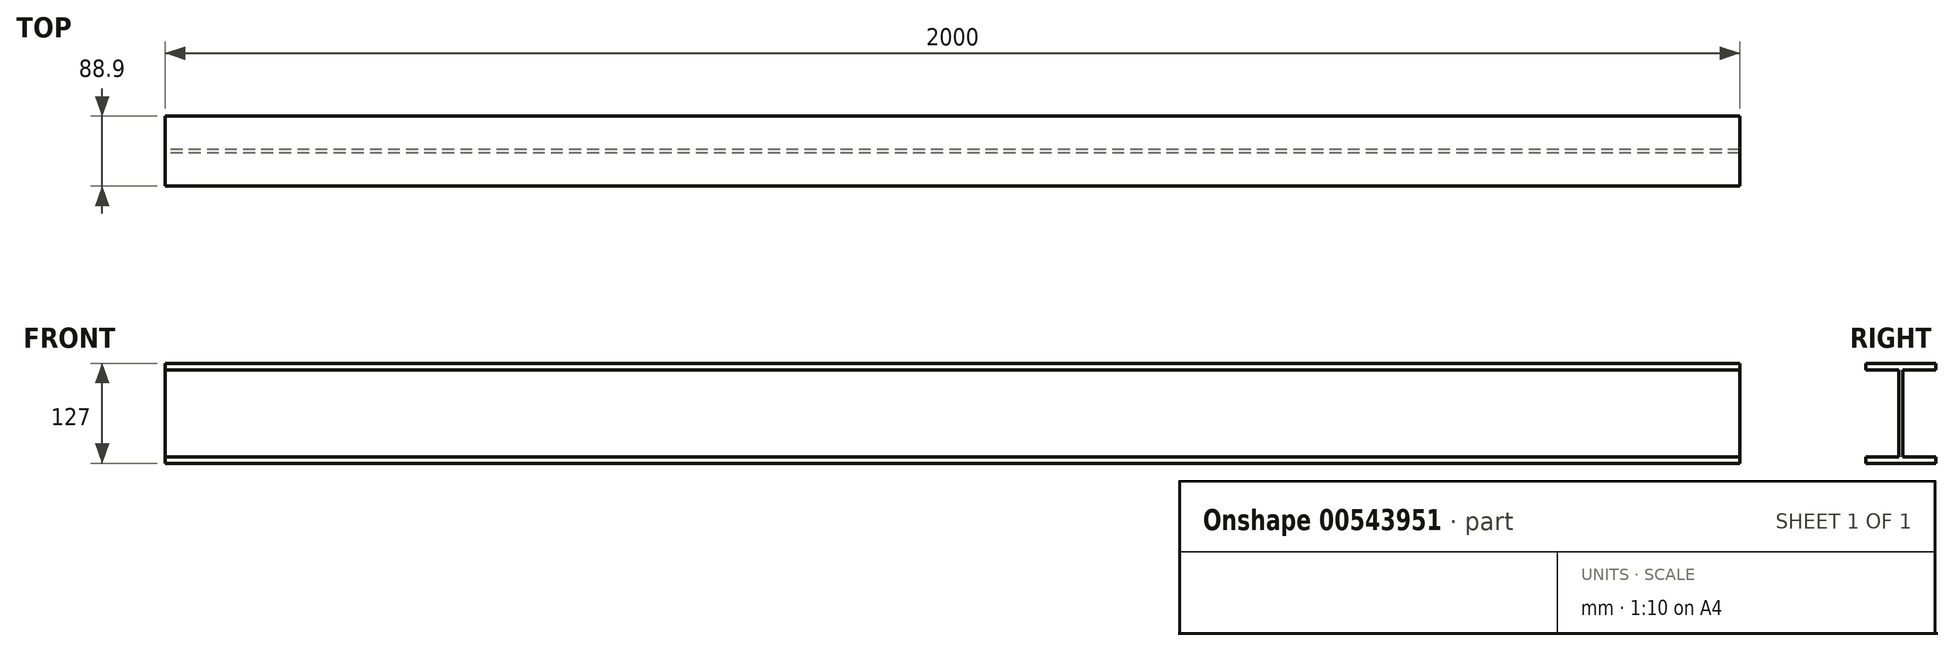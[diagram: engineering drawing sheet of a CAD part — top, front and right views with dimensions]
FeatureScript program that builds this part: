
annotation { "Feature Type Name" : "Feature", "Feature Type Description" : "" }
export const myFeature = defineFeature(function(context is Context, id is Id, definition is map)
    precondition{}
    {
        {
            var Q0;
            Q0=qCreatedBy(makeId("Right.planeOp"),FACE);
            var sketch = newSketch(context, id + "F0", { "sketchPlane" : qUnion([Q0])});
            skLineSegment(sketch, "E0", {"start": v(-44.45, 63.5) * mm, "end": v(44.45, 63.5) * mm});
            skLineSegment(sketch, "E1", {"start": v(44.45, 63.5) * mm, "end": v(44.45, 55.37) * mm});
            skLineSegment(sketch, "E2", {"start": v(44.45, 55.37) * mm, "end": v(2.41, 55.37) * mm});
            skLineSegment(sketch, "E3", {"start": v(2.41, 55.37) * mm, "end": v(2.42, -55.37) * mm});
            skLineSegment(sketch, "E4", {"start": v(2.41, -55.37) * mm, "end": v(44.45, -55.37) * mm});
            skLineSegment(sketch, "E5", {"start": v(44.45, -55.37) * mm, "end": v(44.45, -63.5) * mm});
            skLineSegment(sketch, "E6", {"start": v(44.45, -63.5) * mm, "end": v(-44.45, -63.5) * mm});
            skLineSegment(sketch, "E7", {"start": v(-44.45, -63.5) * mm, "end": v(-44.45, -55.37) * mm});
            skLineSegment(sketch, "E8", {"start": v(-44.45, -55.37) * mm, "end": v(-2.41, -55.37) * mm});
            skLineSegment(sketch, "E9", {"start": v(-2.42, -55.37) * mm, "end": v(-2.42, 55.37) * mm});
            skLineSegment(sketch, "E10", {"start": v(-2.41, 55.37) * mm, "end": v(-44.45, 55.37) * mm});
            skLineSegment(sketch, "E11", {"start": v(-44.45, 55.37) * mm, "end": v(-44.45, 63.5) * mm});
            skSolve(sketch);
        }
        {
            var Q0;
            Q0=makeQuery(id+"F0.imprint","IMPRINT",FACE,{"disambiguationData":[TD([[makeQuery(id+"F0.imprint","IMPRINT",EDGE,{"derivedFrom":sQuery(id+"F0.wireOp",EDGE,"E0")}),-1.0]])]});
            extrude(context, id + "F1", {"entities" : qUnion([Q0]), "depth" : 2000 * mm, "offsetDistance" : 25 * mm});
        }
    });
